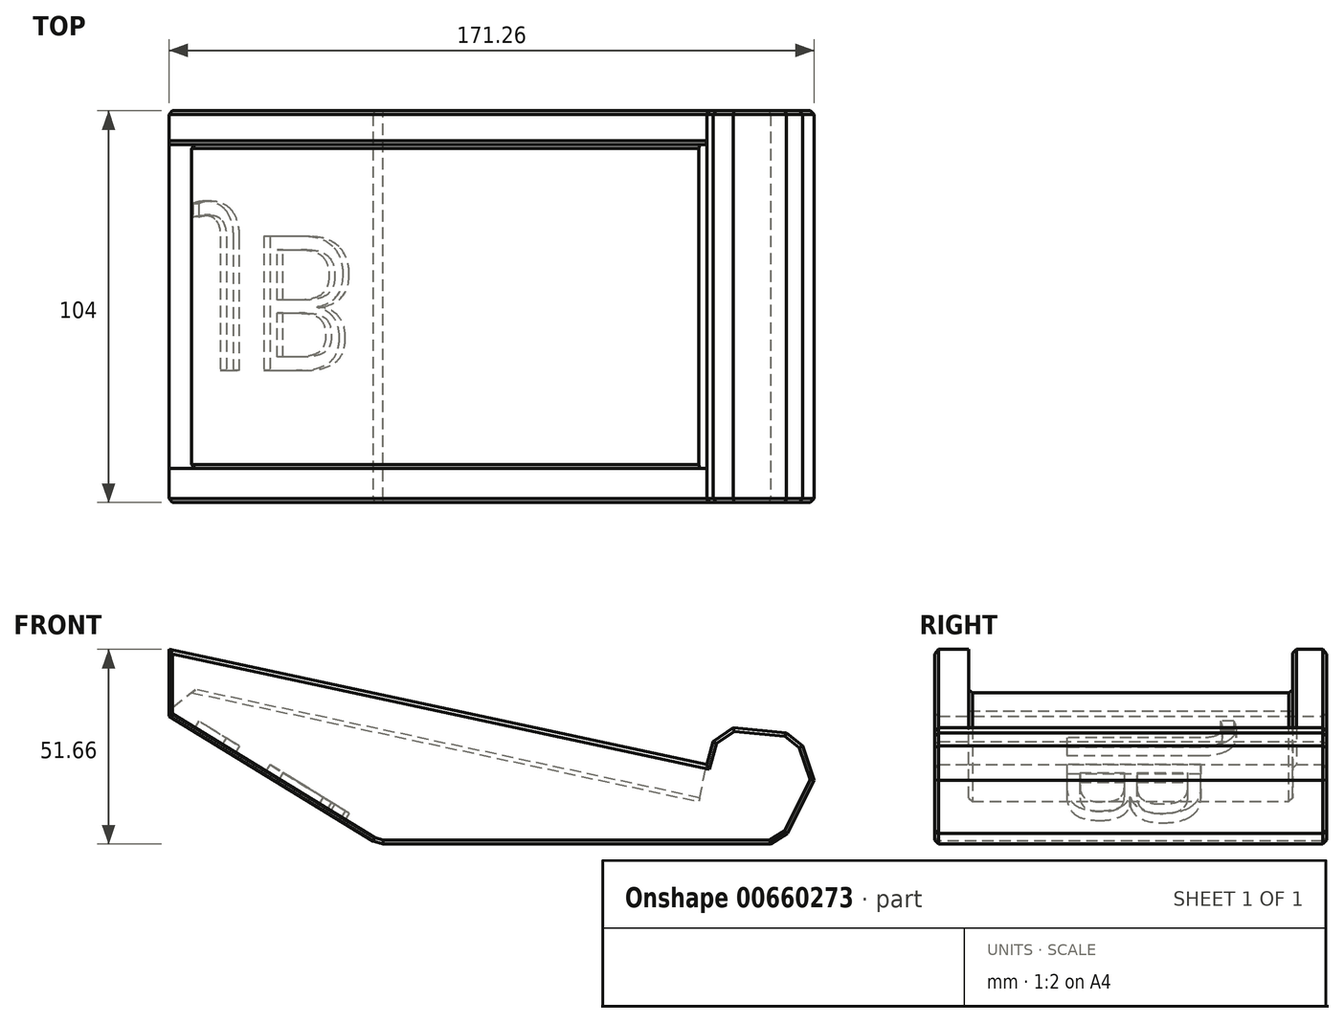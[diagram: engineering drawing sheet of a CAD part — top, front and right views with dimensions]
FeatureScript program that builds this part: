
annotation { "Feature Type Name" : "Feature", "Feature Type Description" : "" }
export const myFeature = defineFeature(function(context is Context, id is Id, definition is map)
    precondition{}
    {
        {
            var Q0;
            Q0=qCreatedBy(makeId("Front.planeOp"),FACE);
            var sketch = newSketch(context, id + "F0", { "sketchPlane" : qUnion([Q0])});
            skLineSegment(sketch, "E0", {"start": v(-90.06, 17.7) * mm, "end": v(-90.06, 0) * mm});
            skLineSegment(sketch, "E1", {"start": v(-90.06, 0) * mm, "end": v(-34.64, -33.96) * mm});
            skLineSegment(sketch, "E2", {"start": v(-34.64, -33.96) * mm, "end": v(72.75, -33.96) * mm});
            skLineSegment(sketch, "E3", {"start": v(72.75, -33.96) * mm, "end": v(81.2, -17.1) * mm});
            skLineSegment(sketch, "E4", {"start": v(81.2, -17.1) * mm, "end": v(77.14, -4.78) * mm});
            skLineSegment(sketch, "E5", {"start": v(77.14, -4.78) * mm, "end": v(55.59, -2.73) * mm});
            skLineSegment(sketch, "E6", {"start": v(55.59, -2.73) * mm, "end": v(52.69, -12.93) * mm});
            skLineSegment(sketch, "E7", {"start": v(52.69, -12.93) * mm, "end": v(-90.06, 17.7) * mm});
            skSolve(sketch);
        }
        {
            var Q0;
            Q0=makeQuery(id+"F0.imprint","IMPRINT",FACE,{"disambiguationData":[TD([[makeQuery(id+"F0.imprint","IMPRINT",EDGE,{"derivedFrom":sQuery(id+"F0.wireOp",EDGE,"E0")}),1.0]])]});
            extrude(context, id + "F1", {"entities" : qUnion([Q0]), "depth" : 52 * mm, "offsetDistance" : 25 * mm, "hasSecondDirection" : true, "secondDirectionOppositeDirection" : true, "secondDirectionDepth" : 52 * mm});
        }
        {
            var Q0;
            Q0=makeQuery(id+"F1.opExtrude","SWEPT_FACE",FACE,{"disambiguationData":[OSD([sQuery(id+"F0.wireOp",EDGE,"E7")])]});
            var sketch = newSketch(context, id + "F2", { "sketchPlane" : qUnion([Q0])});
            skLineSegment(sketch, "E8.bottom", {"start": v(54.23, 43) * mm, "end": v(-119.55, 43) * mm});
            skLineSegment(sketch, "E8.top", {"start": v(54.23, -43) * mm, "end": v(-119.55, -43) * mm});
            skLineSegment(sketch, "E8.left", {"start": v(54.23, 43) * mm, "end": v(54.23, -43) * mm});
            skLineSegment(sketch, "E8.right", {"start": v(-119.55, 43) * mm, "end": v(-119.55, -43) * mm});
            skPoint(sketch, "E8.middle", {"position": v(-32.66, 0) * mm});
            skSolve(sketch);
        }
        {
            var Q0;
            Q0 = qSketchRegion(id + "F2", true);
            var Q1;
            {var subQ0=sQuery(id+"F2.wireOp",EDGE,"E8.left");Q1=makeQuery(id+"F2.imprint","IMPRINT",FACE,{"disambiguationData":[TD([[makeQuery(id+"F2.imprint","IMPRINT",EDGE,{"derivedFrom":subQ0}),1.0]])]});}
            extrude(context, id + "F3", {"entities" : qUnion([Q0, Q1]), "operationType" : NewBodyOperationType.REMOVE, "oppositeDirection" : true, "depth" : 10 * mm, "offsetDistance" : 25 * mm});
        }
        {
            var Q0;
            Q0=makeQuery(id+"F1.opExtrude","SWEPT_FACE",FACE,{"disambiguationData":[OSD([sQuery(id+"F0.wireOp",EDGE,"E1")])]});
            var sketch = newSketch(context, id + "F4", { "sketchPlane" : qUnion([Q0])});
            skText(sketch, "E9", { "text": "JB", "fontName": "OpenSans-Regular.ttf"});
            const initialGuessF4  = {"E9": [-0.06539, -0.0186, 1, 0, 0.0359]};
            skSetInitialGuess(sketch, initialGuessF4);
            skSolve(sketch);
        }
        {
            var Q0;
            Q0 = qSketchRegion(id + "F4", true);
            extrude(context, id + "F5", {"entities" : qUnion([Q0]), "operationType" : NewBodyOperationType.REMOVE, "oppositeDirection" : true, "depth" : 3 * mm, "offsetDistance" : 25 * mm});
        }
        {
            var Q0;
            Q0=makeQuery(id+"F1.opExtrude","SWEPT_EDGE",EDGE,{"disambiguationData":[OSD([sQuery(id+"F0.wireOp",EDGE,"E4"),sQuery(id+"F0.wireOp",EDGE,"E5")])]});
            chamfer(context, id + "F6", {"entities" : qUnion([Q0]), "width" : 5 * mm, "tangentPropagation" : true});
        }
        {
            var Q0;
            Q0=makeQuery(id+"F1.opExtrude","SWEPT_EDGE",EDGE,{"disambiguationData":[OSD([sQuery(id+"F0.wireOp",EDGE,"E5"),sQuery(id+"F0.wireOp",EDGE,"E6")])]});
            chamfer(context, id + "F7", {"entities" : qUnion([Q0]), "width" : 5 * mm, "tangentPropagation" : true});
        }
        {
            var Q0;
            Q0=makeQuery(id+"F1.opExtrude","SWEPT_EDGE",EDGE,{"disambiguationData":[OSD([sQuery(id+"F0.wireOp",EDGE,"E2"),sQuery(id+"F0.wireOp",EDGE,"E3")])]});
            chamfer(context, id + "F8", {"entities" : qUnion([Q0]), "width" : 5 * mm, "tangentPropagation" : true});
        }
        {
            var Q0;
            Q0=makeQuery(id+"F3.boolean.opBoolean","INTERSECT",EDGE,{"derivedFrom":[makeQuery(id+"F1.opExtrude","SWEPT_FACE",FACE,{"disambiguationData":[OSD([sQuery(id+"F0.wireOp",EDGE,"E0")])]}),makeQuery(id+"F3.opExtrude","CAP_FACE",FACE,{"disambiguationData":[OSD([sQuery(id+"F2.wireOp",EDGE,"E8.bottom"),sQuery(id+"F2.wireOp",EDGE,"E8.top"),sQuery(id+"F2.wireOp",EDGE,"E8.left"),sQuery(id+"F2.wireOp",EDGE,"E8.right")])],"isStart":false})]});
            chamfer(context, id + "F9", {"entities" : qUnion([Q0]), "width" : 5 * mm, "tangentPropagation" : true});
        }
        {
            var Q0;
            Q0=makeQuery(id+"F1.opExtrude","SWEPT_EDGE",EDGE,{"disambiguationData":[OSD([sQuery(id+"F0.wireOp",EDGE,"E1"),sQuery(id+"F0.wireOp",EDGE,"E2")])]});
            chamfer(context, id + "F10", {"entities" : qUnion([Q0]), "width" : 5 * mm, "tangentPropagation" : true});
        }
        {
            var Q0;
            Q0=makeQuery(id+"F1.opExtrude","CAP_FACE",FACE,{"disambiguationData":[OSD([sQuery(id+"F0.wireOp",EDGE,"E0"),sQuery(id+"F0.wireOp",EDGE,"E1"),sQuery(id+"F0.wireOp",EDGE,"E2"),sQuery(id+"F0.wireOp",EDGE,"E3"),sQuery(id+"F0.wireOp",EDGE,"E4"),sQuery(id+"F0.wireOp",EDGE,"E5"),sQuery(id+"F0.wireOp",EDGE,"E6"),sQuery(id+"F0.wireOp",EDGE,"E7")])],"isStart":false});
            chamfer(context, id + "F11", {"entities" : qUnion([Q0]), "width" : 1 * mm, "tangentPropagation" : true});
        }
        {
            var Q0;
            Q0=makeQuery(id+"F1.opExtrude","CAP_FACE",FACE,{"disambiguationData":[OSD([sQuery(id+"F0.wireOp",EDGE,"E0"),sQuery(id+"F0.wireOp",EDGE,"E1"),sQuery(id+"F0.wireOp",EDGE,"E2"),sQuery(id+"F0.wireOp",EDGE,"E3"),sQuery(id+"F0.wireOp",EDGE,"E4"),sQuery(id+"F0.wireOp",EDGE,"E5"),sQuery(id+"F0.wireOp",EDGE,"E6"),sQuery(id+"F0.wireOp",EDGE,"E7")])],"isStart":true});
            chamfer(context, id + "F12", {"entities" : qUnion([Q0]), "width" : 1 * mm, "tangentPropagation" : true});
        }
        {
            var Q0;
            Q0=makeQuery(id+"F3.boolean.opBoolean","COPY",EDGE,{"derivedFrom":makeQuery(id+"F3.opExtrude","CAP_EDGE",EDGE,{"disambiguationData":[OSD([sQuery(id+"F2.wireOp",EDGE,"E8.bottom")])],"isStart":false})});
            var Q1;
            Q1=makeQuery(id+"F3.boolean.opBoolean","COPY",EDGE,{"derivedFrom":makeQuery(id+"F3.opExtrude","CAP_EDGE",EDGE,{"disambiguationData":[OSD([sQuery(id+"F2.wireOp",EDGE,"E8.bottom")])],"isStart":true})});
            var Q2;
            Q2=makeQuery(id+"F3.boolean.opBoolean","COPY",EDGE,{"derivedFrom":makeQuery(id+"F3.opExtrude","CAP_EDGE",EDGE,{"disambiguationData":[OSD([sQuery(id+"F2.wireOp",EDGE,"E8.top")])],"isStart":false})});
            var Q3;
            Q3=makeQuery(id+"F3.boolean.opBoolean","COPY",EDGE,{"derivedFrom":makeQuery(id+"F3.opExtrude","CAP_EDGE",EDGE,{"disambiguationData":[OSD([sQuery(id+"F2.wireOp",EDGE,"E8.top")])],"isStart":true})});
            chamfer(context, id + "F13", {"entities" : qUnion([Q0, Q1, Q2, Q3]), "width" : 1 * mm, "tangentPropagation" : true});
        }
    });
